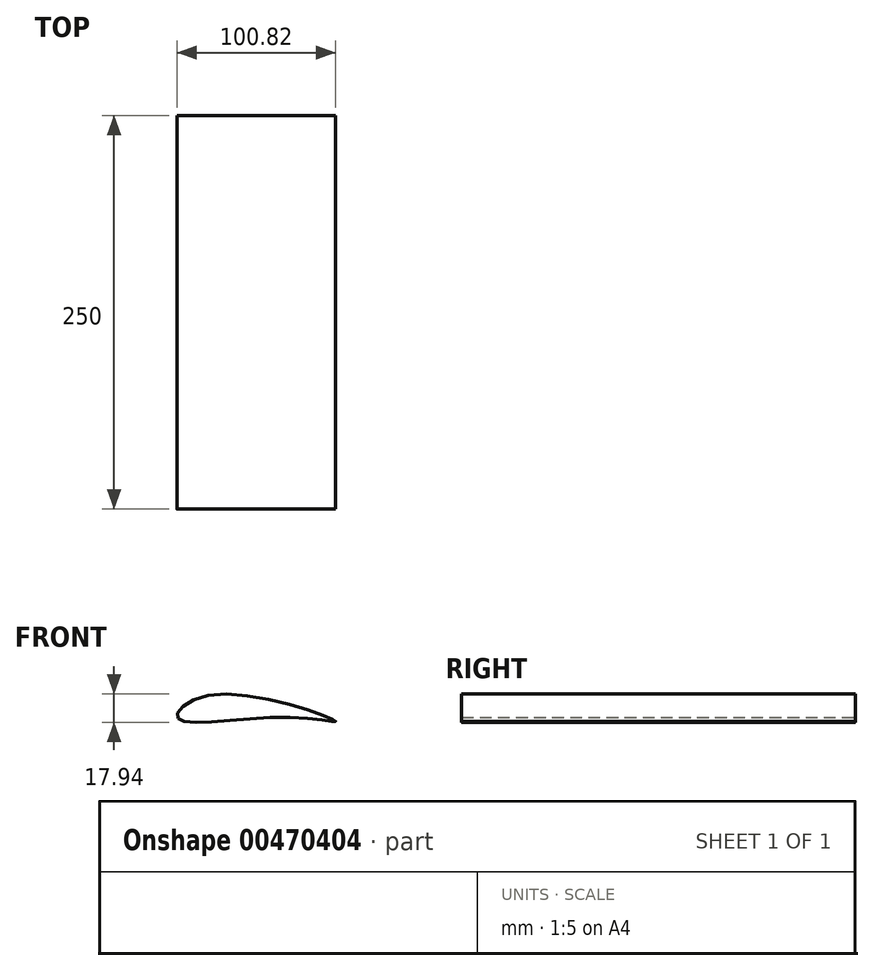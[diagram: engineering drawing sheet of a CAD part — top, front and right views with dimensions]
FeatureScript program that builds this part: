
annotation { "Feature Type Name" : "Feature", "Feature Type Description" : "" }
export const myFeature = defineFeature(function(context is Context, id is Id, definition is map)
    precondition{}
    {
        {
            var Q0;
            Q0=qCreatedBy(makeId("Front.planeOp"),FACE);
            var sketch = newSketch(context, id + "F0", { "sketchPlane" : qUnion([Q0])});
            skFitSpline(sketch, "E0", {"points": [v(-77.35, -19.36) * mm, v(-55.71, -4.43) * mm, v(22.65, -20.85) * mm, v(-7.95, -18.61) * mm, v(-77.35, -19.36) * mm]});
            skSolve(sketch);
        }
        {
            var Q0;
            Q0=makeQuery(id+"F0.imprint","IMPRINT",FACE,{"disambiguationData":[TD([[makeQuery(id+"F0.imprint","IMPRINT",EDGE,{"derivedFrom":sQuery(id+"F0.wireOp",EDGE,"E0")}),-1.0]])]});
            extrude(context, id + "F1", {"entities" : qUnion([Q0]), "depth" : 250 * mm});
        }
    });
